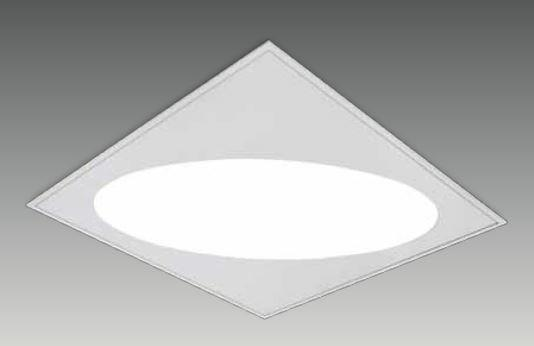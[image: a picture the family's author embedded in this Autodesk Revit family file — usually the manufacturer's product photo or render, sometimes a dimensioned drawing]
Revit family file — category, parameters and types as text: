
# Revit family: G 6060 ELP
name_source: partatom
category: Lighting Fixtures
revit_build: Autodesk Revit 2017 (Build: 20160225_1515(x64)
units: mm (PartAtom-declared; Revit-internal decimal feet)

## family parameters
Always vertical = Yes
Cut with Voids When Loaded = No
Host = Ceiling
Light Source = Yes
OmniClass Number = 23.80.70.11
OmniClass Title = Luminaries for Internal Lighting
Part Type = Normal
Room Calculation Point = No
Round Connector Dimension = Use Diameter
Shared = No

## types (4) — shared parameters
Color Filter = 16777215
Dimming Lamp Color Temperature Shift = <None>
Emit Shape Visible in Rendering = Yes
Emit from Rectangle Length = 560 mm  [stored 1.83727 ft]
Emit from Rectangle Width = 560 mm  [stored 1.83727 ft]
Light Source Symbol Size = 610 mm
Manufacturer = ARLIGHT
Type Image = G 6060 ELP.JPG

## per-type parameters (varying)
| type | Wattage Comments |
| GELP.6060.36.30 | 36 |
| GELP.6060.36.40 | 36 |
| GELP.6060.28.30 | 28 |
| GELP.6060.28.40 | 28 |

note: [stored X ft] marks values corroborated as IEEE doubles in the binary element streams (Revit-internal decimal feet)

## geometry (parser evidence)
native form markers: Sweep x2
no freeform markers — native parametric forms only
